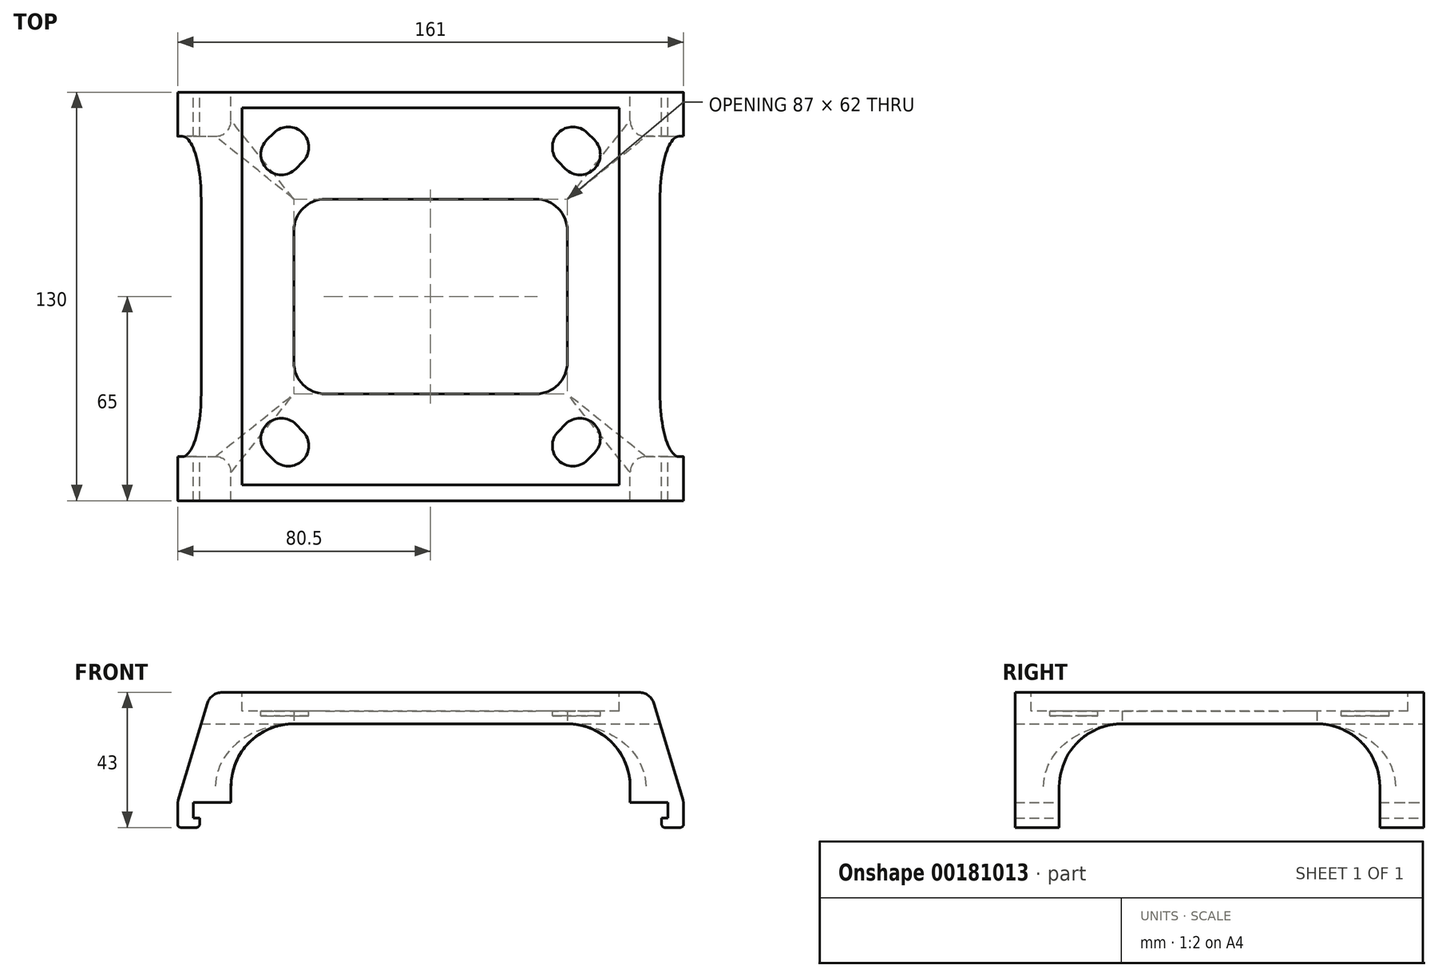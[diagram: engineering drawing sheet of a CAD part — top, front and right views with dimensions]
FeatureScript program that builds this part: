
annotation { "Feature Type Name" : "Feature", "Feature Type Description" : "" }
export const myFeature = defineFeature(function(context is Context, id is Id, definition is map)
    precondition{}
    {
        {
            var Q0;
            Q0=qCreatedBy(makeId("Front.planeOp"),FACE);
            var sketch = newSketch(context, id + "F0", { "sketchPlane" : qUnion([Q0])});
            skLineSegment(sketch, "E0", {"start": v(75.5, 0) * mm, "end": v(75.5, -5) * mm});
            skLineSegment(sketch, "E1", {"start": v(75.5, -5) * mm, "end": v(73.5, -5) * mm});
            skLineSegment(sketch, "E2", {"start": v(73.5, -5) * mm, "end": v(73.5, -7) * mm});
            skLineSegment(sketch, "E3", {"start": v(74.5, -8) * mm, "end": v(79.5, -8) * mm});
            skLineSegment(sketch, "E4", {"start": v(80.5, -7) * mm, "end": v(80.5, -0.73) * mm});
            skLineSegment(sketch, "E5", {"start": v(75.5, 0) * mm, "end": v(63.5, 0) * mm});
            skLineSegment(sketch, "E6", {"start": v(63.5, 0) * mm, "end": v(63.5, 5) * mm});
            skLineSegment(sketch, "E7", {"start": v(0, 25) * mm, "end": v(43.5, 25) * mm});
            skLineSegment(sketch, "E8", {"start": v(66.28, 35) * mm, "end": v(0, 35) * mm});
            skLineSegment(sketch, "E9", {"start": v(80.29, 0.7) * mm, "end": v(71.07, 31.44) * mm});
            skArc(sketch, "E10.filletArc", {"start": v(63.5, 5) * mm, "mid": v(57.64, 19.14) * mm, "end": v(43.5, 25) * mm});
            skPoint(sketch, "E11.visualSharp", {"position": v(70, 35) * mm});
            skArc(sketch, "E11.filletArc", {"start": v(71.07, 31.44) * mm, "mid": v(69.26, 34.01) * mm, "end": v(66.28, 35) * mm});
            skPoint(sketch, "E12.visualSharp", {"position": v(80.5, 0) * mm});
            skArc(sketch, "E12.filletArc", {"start": v(80.5, -0.73) * mm, "mid": v(80.45, 0) * mm, "end": v(80.29, 0.7) * mm});
            skPoint(sketch, "E13.visualSharp", {"position": v(73.5, -8) * mm});
            skArc(sketch, "E13.filletArc", {"start": v(73.5, -7) * mm, "mid": v(73.8, -7.7) * mm, "end": v(74.5, -8) * mm});
            skPoint(sketch, "E14.visualSharp", {"position": v(80.5, -8) * mm});
            skArc(sketch, "E14.filletArc", {"start": v(79.5, -8) * mm, "mid": v(80.2, -7.7) * mm, "end": v(80.5, -7) * mm});
            skLineSegment(sketch, "E15.MirrorCS", {"start": v(-75.5, -5) * mm, "end": v(-73.5, -5) * mm});
            skArc(sketch, "E16.MirrorCS", {"start": v(-79.5, -8) * mm, "mid": v(-80.2, -7.7) * mm, "end": v(-80.5, -7) * mm});
            skArc(sketch, "E17.MirrorCS", {"start": v(-73.5, -7) * mm, "mid": v(-73.8, -7.7) * mm, "end": v(-74.5, -8) * mm});
            skLineSegment(sketch, "E18.MirrorCS", {"start": v(-73.5, -5) * mm, "end": v(-73.5, -7) * mm});
            skArc(sketch, "E19.MirrorCS", {"start": v(-80.5, -0.73) * mm, "mid": v(-80.45, 0) * mm, "end": v(-80.29, 0.7) * mm});
            skArc(sketch, "E20.MirrorCS", {"start": v(-71.07, 31.44) * mm, "mid": v(-69.26, 34.01) * mm, "end": v(-66.28, 35) * mm});
            skLineSegment(sketch, "E21.MirrorCS", {"start": v(0, 25) * mm, "end": v(-43.5, 25) * mm});
            skPoint(sketch, "E22.MirrorP", {"position": v(-73.5, -8) * mm});
            skLineSegment(sketch, "E23.MirrorCS", {"start": v(-74.5, -8) * mm, "end": v(-79.5, -8) * mm});
            skPoint(sketch, "E24.MirrorP", {"position": v(-80.5, 0) * mm});
            skLineSegment(sketch, "E25.MirrorCS", {"start": v(-66.28, 35) * mm, "end": v(0, 35) * mm});
            skPoint(sketch, "E26.MirrorP", {"position": v(-70, 35) * mm});
            skPoint(sketch, "E27.MirrorP", {"position": v(-80.5, -8) * mm});
            skLineSegment(sketch, "E28.MirrorCS", {"start": v(-75.5, 0) * mm, "end": v(-75.5, -5) * mm});
            skLineSegment(sketch, "E29.MirrorCS", {"start": v(-63.5, 0) * mm, "end": v(-63.5, 5) * mm});
            skLineSegment(sketch, "E30.MirrorCS", {"start": v(-80.5, -7) * mm, "end": v(-80.5, -0.73) * mm});
            skLineSegment(sketch, "E31.MirrorCS", {"start": v(-75.5, 0) * mm, "end": v(-63.5, 0) * mm});
            skLineSegment(sketch, "E32.MirrorCS", {"start": v(-80.29, 0.7) * mm, "end": v(-71.07, 31.44) * mm});
            skArc(sketch, "E33.MirrorCS", {"start": v(-63.5, 5) * mm, "mid": v(-57.64, 19.14) * mm, "end": v(-43.5, 25) * mm});
            skSolve(sketch);
        }
        {
            var Q0;
            Q0=makeQuery(id+"F0.imprint","IMPRINT",FACE,{"disambiguationData":[TD([[makeQuery(id+"F0.imprint","IMPRINT",EDGE,{"derivedFrom":sQuery(id+"F0.wireOp",EDGE,"E0")}),1.0]])]});
            extrude(context, id + "F1", {"entities" : qUnion([Q0]), "endBound" : BoundingType.SYMMETRIC, "depth" : 130 * mm});
        }
        {
            var Q0;
            Q0=makeQuery(id+"F1.opExtrude","SWEPT_FACE",FACE,{"disambiguationData":[OSD([sQuery(id+"F0.wireOp",EDGE,"E4")])]});
            var sketch = newSketch(context, id + "F2", { "sketchPlane" : qUnion([Q0])});
            skLineSegment(sketch, "E34.bottom", {"start": v(51, 25) * mm, "end": v(-51, 25) * mm});
            skLineSegment(sketch, "E34.top", {"start": v(51, -25) * mm, "end": v(-51, -25) * mm});
            skLineSegment(sketch, "E34.left", {"start": v(51, 5) * mm, "end": v(51, -25) * mm});
            skLineSegment(sketch, "E34.right", {"start": v(-51, 5) * mm, "end": v(-51, -25) * mm});
            skPoint(sketch, "E34.middle", {"position": v(0, 0) * mm});
            skLineSegment(sketch, "E35.0", {"start": v(65, -7) * mm, "end": v(65, -0.73) * mm});
            skLineSegment(sketch, "E36.0.1", {"start": v(65, 25) * mm, "end": v(-65, 25) * mm});
            skLineSegment(sketch, "E36.0.3", {"start": v(-31, 25) * mm, "end": v(31, 25) * mm});
            skPoint(sketch, "E37.newPointA", {"position": v(-65, 25) * mm});
            skArc(sketch, "E37.filletArc", {"start": v(-31, 25) * mm, "mid": v(-45.14, 19.14) * mm, "end": v(-51, 5) * mm});
            skPoint(sketch, "E38.newPointA", {"position": v(65, 25) * mm});
            skArc(sketch, "E38.filletArc", {"start": v(51, 5) * mm, "mid": v(45.14, 19.14) * mm, "end": v(31, 25) * mm});
            skSolve(sketch);
        }
        {
            var Q0;
            Q0 = qSketchRegion(id + "F2", true);
            extrude(context, id + "F3", {"entities" : qUnion([Q0]), "operationType" : NewBodyOperationType.REMOVE, "endBound" : BoundingType.THROUGH_ALL, "oppositeDirection" : true, "depth" : 25 * mm});
        }
        {
            var Q0;
            Q0=makeQuery(id+"F1.opExtrude","SWEPT_FACE",FACE,{"disambiguationData":[OSD([sQuery(id+"F0.wireOp",EDGE,"E8"),sQuery(id+"F0.wireOp",EDGE,"E25.MirrorCS")])]});
            var sketch = newSketch(context, id + "F4", { "sketchPlane" : qUnion([Q0])});
            skLineSegment(sketch, "E39.bottom", {"start": v(60, 60) * mm, "end": v(-60, 60) * mm});
            skLineSegment(sketch, "E39.top", {"start": v(60, -60) * mm, "end": v(-60, -60) * mm});
            skLineSegment(sketch, "E39.left", {"start": v(60, 60) * mm, "end": v(60, -60) * mm});
            skLineSegment(sketch, "E39.right", {"start": v(-60, 60) * mm, "end": v(-60, -60) * mm});
            skPoint(sketch, "E39.middle", {"position": v(0, 0) * mm});
            skSolve(sketch);
        }
        {
            var Q0;
            Q0=makeQuery(id+"F4.imprint","IMPRINT",FACE,{"disambiguationData":[TD([[makeQuery(id+"F4.imprint","IMPRINT",EDGE,{"derivedFrom":sQuery(id+"F4.wireOp",EDGE,"E39.bottom")}),1.0]])]});
            extrude(context, id + "F5", {"entities" : qUnion([Q0]), "operationType" : NewBodyOperationType.REMOVE, "oppositeDirection" : true, "depth" : 6 * mm});
        }
        {
            var Q0;
            Q0=makeQuery(id+"F5.boolean.opBoolean","COPY",FACE,{"derivedFrom":makeQuery(id+"F5.opExtrude","CAP_FACE",FACE,{"disambiguationData":[OSD([sQuery(id+"F4.wireOp",EDGE,"E39.bottom"),sQuery(id+"F4.wireOp",EDGE,"E39.top"),sQuery(id+"F4.wireOp",EDGE,"E39.left"),sQuery(id+"F4.wireOp",EDGE,"E39.right")])],"isStart":false})});
            var sketch = newSketch(context, id + "F6", { "sketchPlane" : qUnion([Q0])});
            skArc(sketch, "E40", {"start": v(52.1, -49.85) * mm, "mid": v(52.1, -40.65) * mm, "end": v(42.9, -40.65) * mm});
            skLineSegment(sketch, "E41", {"start": v(47.5, -127.9) * mm, "end": v(47.5, 109.28) * mm, "construction": true});
            skLineSegment(sketch, "E42", {"start": v(45.25, 108.61) * mm, "end": v(45.25, -109.3) * mm, "construction": true});
            skLineSegment(sketch, "E43", {"start": v(116.9, -47.5) * mm, "end": v(-134.83, -47.5) * mm, "construction": true});
            skLineSegment(sketch, "E44", {"start": v(118.53, -45.25) * mm, "end": v(-134.83, -45.25) * mm, "construction": true});
            skLineSegment(sketch, "E45", {"start": v(-134.83, -45.25) * mm, "end": v(-137.68, -44.44) * mm, "construction": true});
            skArc(sketch, "E46", {"start": v(40.65, -42.9) * mm, "mid": v(40.65, -52.1) * mm, "end": v(49.85, -52.1) * mm});
            skLineSegment(sketch, "E47", {"start": v(42.9, -40.65) * mm, "end": v(40.65, -42.9) * mm});
            skLineSegment(sketch, "E48", {"start": v(52.1, -49.85) * mm, "end": v(49.85, -52.1) * mm});
            skLineSegment(sketch, "E49.MirrorCS", {"start": v(52.1, 49.85) * mm, "end": v(49.85, 52.1) * mm});
            skLineSegment(sketch, "E50.MirrorCS", {"start": v(42.9, 40.65) * mm, "end": v(40.65, 42.9) * mm});
            skArc(sketch, "E51.MirrorCS", {"start": v(40.65, 42.9) * mm, "mid": v(40.65, 52.1) * mm, "end": v(49.85, 52.1) * mm});
            skLineSegment(sketch, "E52.MirrorCS", {"start": v(45.25, -108.61) * mm, "end": v(45.25, 109.3) * mm, "construction": true});
            skLineSegment(sketch, "E53.MirrorCS", {"start": v(118.53, 45.25) * mm, "end": v(-134.83, 45.25) * mm, "construction": true});
            skLineSegment(sketch, "E54.MirrorCS", {"start": v(116.9, 47.5) * mm, "end": v(-134.83, 47.5) * mm, "construction": true});
            skArc(sketch, "E55.MirrorCS", {"start": v(52.1, 49.85) * mm, "mid": v(52.1, 40.65) * mm, "end": v(42.9, 40.65) * mm});
            skLineSegment(sketch, "E56.MirrorCS", {"start": v(47.5, 127.9) * mm, "end": v(47.5, -109.28) * mm, "construction": true});
            skLineSegment(sketch, "E57.MirrorCS", {"start": v(-42.9, 40.65) * mm, "end": v(-40.65, 42.9) * mm});
            skLineSegment(sketch, "E58.MirrorCS", {"start": v(-52.1, 49.85) * mm, "end": v(-49.85, 52.1) * mm});
            skArc(sketch, "E59.MirrorCS", {"start": v(-52.1, 49.85) * mm, "mid": v(-52.1, 40.65) * mm, "end": v(-42.9, 40.65) * mm});
            skArc(sketch, "E60.MirrorCS", {"start": v(-40.65, 42.9) * mm, "mid": v(-40.65, 52.1) * mm, "end": v(-49.85, 52.1) * mm});
            skLineSegment(sketch, "E61.MirrorCS", {"start": v(-42.9, -40.65) * mm, "end": v(-40.65, -42.9) * mm});
            skArc(sketch, "E62.MirrorCS", {"start": v(-40.65, -42.9) * mm, "mid": v(-40.65, -52.1) * mm, "end": v(-49.85, -52.1) * mm});
            skLineSegment(sketch, "E63.MirrorCS", {"start": v(-52.1, -49.85) * mm, "end": v(-49.85, -52.1) * mm});
            skArc(sketch, "E64.MirrorCS", {"start": v(-52.1, -49.85) * mm, "mid": v(-52.1, -40.65) * mm, "end": v(-42.9, -40.65) * mm});
            skSolve(sketch);
        }
        {
            var Q0;
            Q0 = qSketchRegion(id + "F6", true);
            extrude(context, id + "F7", {"entities" : qUnion([Q0]), "operationType" : NewBodyOperationType.REMOVE, "oppositeDirection" : true, "depth" : 1.5 * mm});
        }
        {
            var Q0;
            Q0=makeQuery(id+"F3.boolean.opBoolean","MERGE",FACE,{"derivedFrom":[makeQuery(id+"F1.opExtrude","SWEPT_FACE",FACE,{"disambiguationData":[OSD([sQuery(id+"F0.wireOp",EDGE,"E7"),sQuery(id+"F0.wireOp",EDGE,"E21.MirrorCS")])]}),makeQuery(id+"F3.opExtrude","SWEPT_FACE",FACE,{"disambiguationData":[OSD([sQuery(id+"F2.wireOp",EDGE,"E36.0.3")])]})]});
            var sketch = newSketch(context, id + "F8", { "sketchPlane" : qUnion([Q0])});
            skLineSegment(sketch, "E65.bottom", {"start": v(33.5, -31) * mm, "end": v(-33.5, -31) * mm});
            skLineSegment(sketch, "E65.top", {"start": v(33.5, 31) * mm, "end": v(-33.5, 31) * mm});
            skLineSegment(sketch, "E65.left", {"start": v(43.5, -21) * mm, "end": v(43.5, 21) * mm});
            skLineSegment(sketch, "E65.right", {"start": v(-43.5, -21) * mm, "end": v(-43.5, 21) * mm});
            skPoint(sketch, "E65.middle", {"position": v(0, 0) * mm});
            skPoint(sketch, "E66.visualSharp", {"position": v(43.5, 31) * mm});
            skArc(sketch, "E66.filletArc", {"start": v(43.5, 21) * mm, "mid": v(40.57, 28.07) * mm, "end": v(33.5, 31) * mm});
            skPoint(sketch, "E67.visualSharp", {"position": v(43.5, -31) * mm});
            skArc(sketch, "E67.filletArc", {"start": v(33.5, -31) * mm, "mid": v(40.57, -28.07) * mm, "end": v(43.5, -21) * mm});
            skPoint(sketch, "E68.visualSharp", {"position": v(-43.5, -31) * mm});
            skArc(sketch, "E68.filletArc", {"start": v(-43.5, -21) * mm, "mid": v(-40.57, -28.07) * mm, "end": v(-33.5, -31) * mm});
            skPoint(sketch, "E69.visualSharp", {"position": v(-43.5, 31) * mm});
            skArc(sketch, "E69.filletArc", {"start": v(-33.5, 31) * mm, "mid": v(-40.57, 28.07) * mm, "end": v(-43.5, 21) * mm});
            skSolve(sketch);
        }
        {
            var Q0;
            Q0=makeQuery(id+"F8.imprint","IMPRINT",FACE,{"disambiguationData":[TD([[makeQuery(id+"F8.imprint","IMPRINT",EDGE,{"derivedFrom":sQuery(id+"F8.wireOp",EDGE,"E65.bottom")}),-1.0]])]});
            extrude(context, id + "F9", {"entities" : qUnion([Q0]), "operationType" : NewBodyOperationType.REMOVE, "endBound" : BoundingType.THROUGH_ALL, "oppositeDirection" : true, "depth" : 25 * mm});
        }
        {
            var Q0;
            Q0=makeQuery(id+"F3.boolean.opBoolean","INTERSECT",EDGE,{"derivedFrom":[makeQuery(id+"F1.opExtrude","SWEPT_FACE",FACE,{"disambiguationData":[OSD([sQuery(id+"F0.wireOp",EDGE,"E33.MirrorCS")])]}),makeQuery(id+"F3.opExtrude","SWEPT_FACE",FACE,{"disambiguationData":[OSD([sQuery(id+"F2.wireOp",EDGE,"E38.filletArc")])]})]});
            var Q1;
            Q1=makeQuery(id+"F3.boolean.opBoolean","INTERSECT",EDGE,{"derivedFrom":[makeQuery(id+"F1.opExtrude","SWEPT_FACE",FACE,{"disambiguationData":[OSD([sQuery(id+"F0.wireOp",EDGE,"E33.MirrorCS")])]}),makeQuery(id+"F3.opExtrude","SWEPT_FACE",FACE,{"disambiguationData":[OSD([sQuery(id+"F2.wireOp",EDGE,"E37.filletArc")])]})]});
            var Q2;
            Q2=makeQuery(id+"F3.boolean.opBoolean","INTERSECT",EDGE,{"derivedFrom":[makeQuery(id+"F1.opExtrude","SWEPT_FACE",FACE,{"disambiguationData":[OSD([sQuery(id+"F0.wireOp",EDGE,"E10.filletArc")])]}),makeQuery(id+"F3.opExtrude","SWEPT_FACE",FACE,{"disambiguationData":[OSD([sQuery(id+"F2.wireOp",EDGE,"E37.filletArc")])]})]});
            var Q3;
            Q3=makeQuery(id+"F3.boolean.opBoolean","INTERSECT",EDGE,{"derivedFrom":[makeQuery(id+"F1.opExtrude","SWEPT_FACE",FACE,{"disambiguationData":[OSD([sQuery(id+"F0.wireOp",EDGE,"E10.filletArc")])]}),makeQuery(id+"F3.opExtrude","SWEPT_FACE",FACE,{"disambiguationData":[OSD([sQuery(id+"F2.wireOp",EDGE,"E38.filletArc")])]})]});
            fillet(context, id + "F10", {"entities" : qUnion([Q0, Q1, Q2, Q3]), "radius" : 5 * mm, "tangentPropagation" : true, "allowEdgeOverflow" : false});
        }
    });
